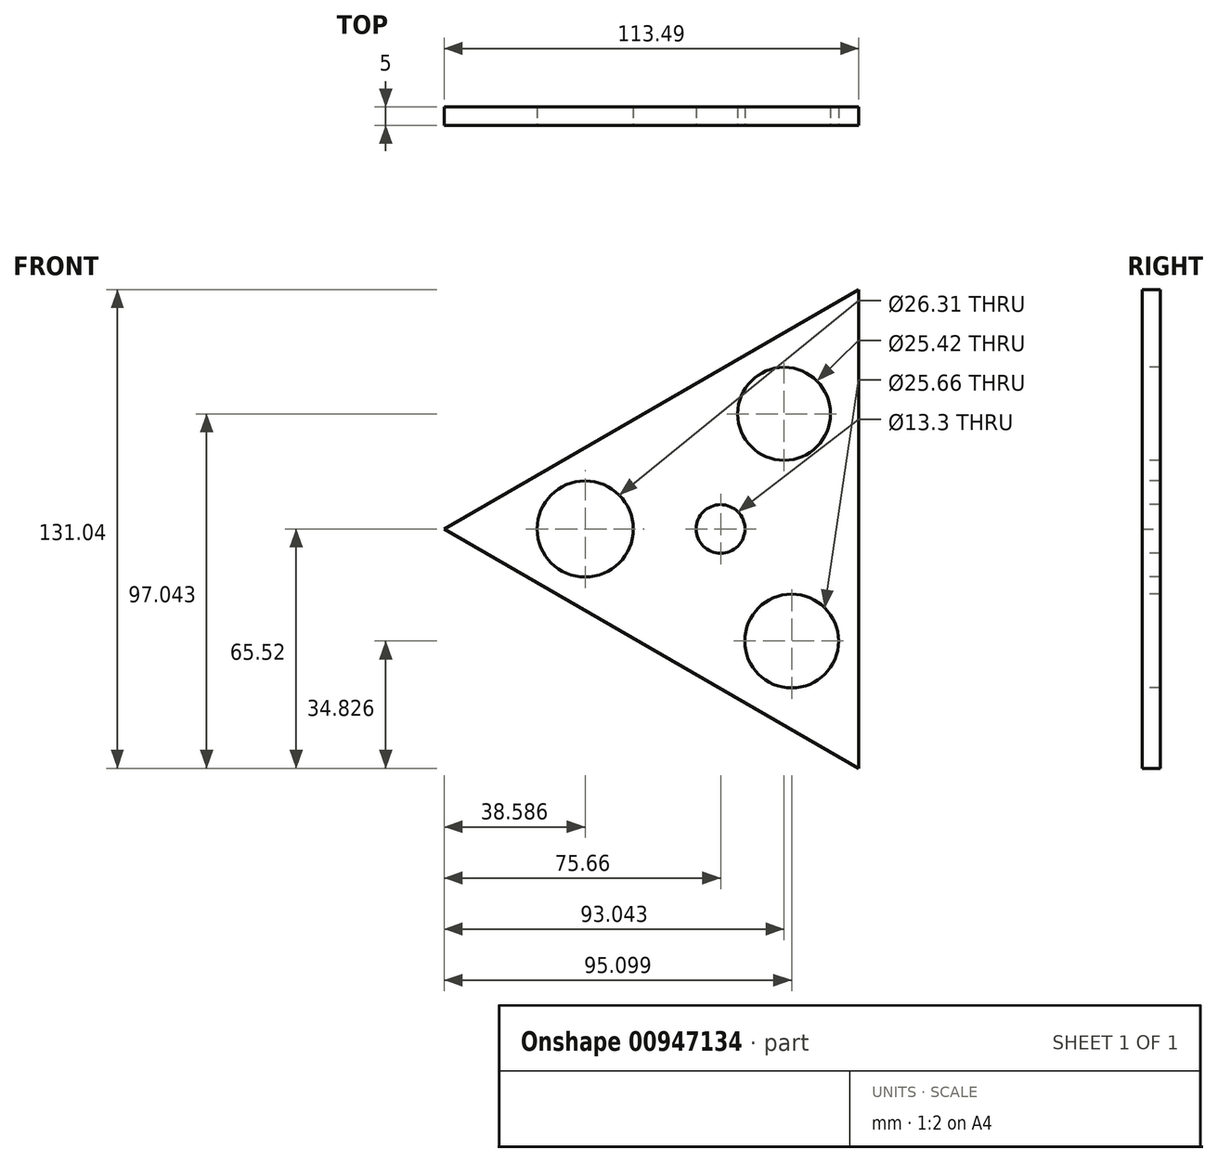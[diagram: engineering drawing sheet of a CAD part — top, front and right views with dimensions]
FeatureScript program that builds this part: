
annotation { "Feature Type Name" : "Feature", "Feature Type Description" : "" }
export const myFeature = defineFeature(function(context is Context, id is Id, definition is map)
    precondition{}
    {
        {
            var Q0;
            Q0=qCreatedBy(makeId("Front.planeOp"),FACE);
            var sketch = newSketch(context, id + "F0", { "sketchPlane" : qUnion([Q0])});
            skCircle(sketch, "E0.cCircle", {"center": v(0, 0) * mm, "radius": 37.83 * mm, "construction": true});
            skLineSegment(sketch, "E0.0", {"start": v(37.83, 65.52) * mm, "end": v(37.83, -65.52) * mm});
            skLineSegment(sketch, "E0.1", {"start": v(37.83, -65.52) * mm, "end": v(-75.66, 0) * mm});
            skLineSegment(sketch, "E0.2", {"start": v(-75.66, 0) * mm, "end": v(37.83, 65.52) * mm});
            skPoint(sketch, "E0.0.midPoint", {"position": v(37.83, 0) * mm});
            skSolve(sketch);
        }
        {
            var Q0;
            Q0=makeQuery(id+"F0.imprint","IMPRINT",FACE,{"disambiguationData":[TD([[makeQuery(id+"F0.imprint","IMPRINT",EDGE,{"derivedFrom":sQuery(id+"F0.wireOp",EDGE,"E0.0")}),-1.0]])]});
            extrude(context, id + "F1", {"entities" : qUnion([Q0]), "depth" : 5 * mm, "offsetDistance" : 25.4 * mm});
        }
        {
            var Q0;
            Q0=makeQuery(id+"F1.opExtrude","CAP_FACE",FACE,{"disambiguationData":[OSD([sQuery(id+"F0.wireOp",EDGE,"E0.0"),sQuery(id+"F0.wireOp",EDGE,"E0.1"),sQuery(id+"F0.wireOp",EDGE,"E0.2")])],"isStart":false});
            var sketch = newSketch(context, id + "F2", { "sketchPlane" : qUnion([Q0])});
            skCircle(sketch, "E1", {"center": v(-37.07, 0) * mm, "radius": 13.15 * mm});
            skCircle(sketch, "E2", {"center": v(17.17, -30.76) * mm, "radius": 12.92 * mm});
            skSolve(sketch);
        }
        {
            var Q0;
            Q0=makeQuery(id+"F2.imprint","IMPRINT",FACE,{"disambiguationData":[TD([[makeQuery(id+"F2.imprint","IMPRINT",EDGE,{"derivedFrom":sQuery(id+"F2.wireOp",EDGE,"E1")}),-1.0]])]});
            var sketch = newSketch(context, id + "F3", { "sketchPlane" : qUnion([Q0])});
            skCircle(sketch, "E3", {"center": v(17.38, 31.52) * mm, "radius": 12.71 * mm});
            skSolve(sketch);
        }
        {
            var Q0;
            Q0=makeQuery(id+"F2.imprint","IMPRINT",FACE,{"disambiguationData":[TD([[makeQuery(id+"F2.imprint","IMPRINT",EDGE,{"derivedFrom":sQuery(id+"F2.wireOp",EDGE,"E1")}),1.0]])]});
            var Q1;
            Q1=sQuery(id+"F2.wireOp",EDGE,"E1");
            extrude(context, id + "F4", {"entities" : qUnion([Q0]), "operationType" : NewBodyOperationType.REMOVE, "surfaceEntities" : qUnion([Q1]), "oppositeDirection" : true, "depth" : 51.56 * mm, "offsetDistance" : 25.4 * mm});
        }
        {
            var Q0;
            Q0=makeQuery(id+"F3.imprint","IMPRINT",FACE,{"disambiguationData":[TD([[makeQuery(id+"F3.imprint","IMPRINT",EDGE,{"derivedFrom":sQuery(id+"F3.wireOp",EDGE,"E3")}),1.0]])]});
            extrude(context, id + "F5", {"entities" : qUnion([Q0]), "operationType" : NewBodyOperationType.REMOVE, "oppositeDirection" : true, "depth" : 34.3 * mm, "offsetDistance" : 25.4 * mm});
        }
        {
            var Q0;
            Q0=makeQuery(id+"F1.opExtrude","CAP_FACE",FACE,{"disambiguationData":[OSD([sQuery(id+"F0.wireOp",EDGE,"E0.0"),sQuery(id+"F0.wireOp",EDGE,"E0.1"),sQuery(id+"F0.wireOp",EDGE,"E0.2")])],"isStart":false});
            var sketch = newSketch(context, id + "F6", { "sketchPlane" : qUnion([Q0])});
            skCircle(sketch, "E4", {"center": v(19.44, -30.7) * mm, "radius": 12.83 * mm});
            skSolve(sketch);
        }
        {
            var Q0;
            Q0=makeQuery(id+"F6.imprint","IMPRINT",FACE,{"disambiguationData":[TD([[makeQuery(id+"F6.imprint","IMPRINT",EDGE,{"derivedFrom":sQuery(id+"F6.wireOp",EDGE,"E4")}),1.0]])]});
            var Q1;
            Q1=sQuery(id+"F6.wireOp",EDGE,"E4");
            extrude(context, id + "F7", {"entities" : qUnion([Q0]), "operationType" : NewBodyOperationType.REMOVE, "surfaceEntities" : qUnion([Q1]), "oppositeDirection" : true, "depth" : 49.28 * mm, "offsetDistance" : 25.4 * mm});
        }
        {
            var Q0;
            Q0=makeQuery(id+"F1.opExtrude","CAP_FACE",FACE,{"disambiguationData":[OSD([sQuery(id+"F0.wireOp",EDGE,"E0.0"),sQuery(id+"F0.wireOp",EDGE,"E0.1"),sQuery(id+"F0.wireOp",EDGE,"E0.2")])],"isStart":false});
            var sketch = newSketch(context, id + "F8", { "sketchPlane" : qUnion([Q0])});
            skSolve(sketch);
        }
        {
            var Q0;
            Q0=makeQuery(id+"F8.imprint","IMPRINT",FACE,{"disambiguationData":[TD([[makeQuery(id+"F8.imprint","IMPRINT",EDGE,{"derivedFrom":makeQuery(id+"F1.opExtrude","CAP_EDGE",EDGE,{"disambiguationData":[OSD([sQuery(id+"F0.wireOp",EDGE,"E0.0")])],"isStart":false})}),-1.0]])]});
            var sketch = newSketch(context, id + "F9", { "sketchPlane" : qUnion([Q0])});
            skCircle(sketch, "E5", {"center": v(0, 0) * mm, "radius": 6.65 * mm});
            skSolve(sketch);
        }
        {
            var Q0;
            Q0=makeQuery(id+"F9.imprint","IMPRINT",FACE,{"disambiguationData":[TD([[makeQuery(id+"F9.imprint","IMPRINT",EDGE,{"derivedFrom":sQuery(id+"F9.wireOp",EDGE,"E5")}),1.0]])]});
            extrude(context, id + "F10", {"entities" : qUnion([Q0]), "operationType" : NewBodyOperationType.REMOVE, "oppositeDirection" : true, "depth" : 25.4 * mm, "offsetDistance" : 25.4 * mm});
        }
    });
